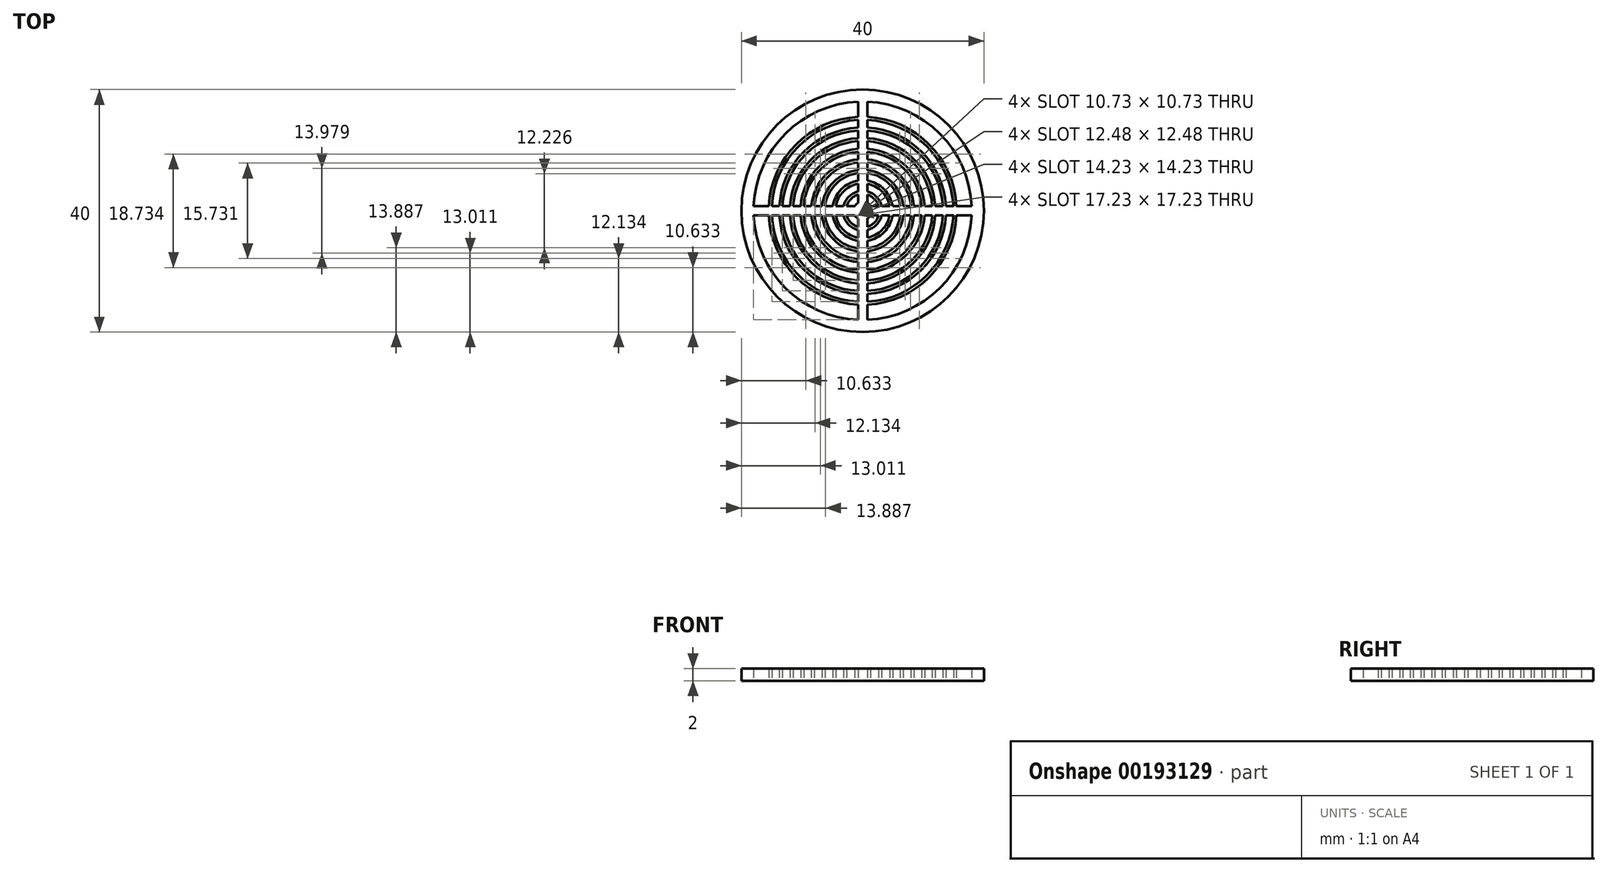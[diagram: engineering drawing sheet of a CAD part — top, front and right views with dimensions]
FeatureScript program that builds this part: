
annotation { "Feature Type Name" : "Feature", "Feature Type Description" : "" }
export const myFeature = defineFeature(function(context is Context, id is Id, definition is map)
    precondition{}
    {
        {
            var Q0;
            Q0=qCreatedBy(makeId("Top.planeOp"),FACE);
            var sketch = newSketch(context, id + "F0", { "sketchPlane" : qUnion([Q0])});
            skArc(sketch, "E0", {"start": v(0.75, -4.94) * mm, "mid": v(3.54, -3.54) * mm, "end": v(4.94, -0.75) * mm});
            skArc(sketch, "E1", {"start": v(0.75, -6.2) * mm, "mid": v(4.42, -4.42) * mm, "end": v(6.2, -0.75) * mm});
            skArc(sketch, "E2", {"start": v(0.75, -4.44) * mm, "mid": v(3.18, -3.18) * mm, "end": v(4.44, -0.75) * mm});
            skArc(sketch, "E3", {"start": v(0.75, -3.16) * mm, "mid": v(2.3, -2.3) * mm, "end": v(3.16, -0.75) * mm});
            skArc(sketch, "E4", {"start": v(0.75, -2.65) * mm, "mid": v(1.94, -1.94) * mm, "end": v(2.65, -0.75) * mm});
            skArc(sketch, "E5", {"start": v(0.75, -1.3) * mm, "mid": v(1.06, -1.06) * mm, "end": v(1.3, -0.75) * mm});
            skArc(sketch, "E6", {"start": v(0.75, -6.7) * mm, "mid": v(4.77, -4.77) * mm, "end": v(6.7, -0.75) * mm});
            skCircle(sketch, "E7", {"center": v(0, 0) * mm, "radius": 20 * mm});
            skLineSegment(sketch, "E8", {"start": v(-0.75, -17.98) * mm, "end": v(-0.75, -15.48) * mm});
            skLineSegment(sketch, "E9", {"start": v(-17.98, 0.75) * mm, "end": v(-15.48, 0.75) * mm});
            skLineSegment(sketch, "E10", {"start": v(34, 0.75) * mm, "end": v(34, -0.75) * mm});
            skLineSegment(sketch, "E11", {"start": v(34, -0.75) * mm, "end": v(19.99, -0.75) * mm});
            skArc(sketch, "E12", {"start": v(0.75, -7.96) * mm, "mid": v(5.66, -5.66) * mm, "end": v(7.96, -0.75) * mm});
            skArc(sketch, "E13", {"start": v(0.75, -8.47) * mm, "mid": v(6.01, -6.01) * mm, "end": v(8.47, -0.75) * mm});
            skArc(sketch, "E14", {"start": v(0.75, -9.72) * mm, "mid": v(6.9, -6.9) * mm, "end": v(9.72, -0.75) * mm});
            skArc(sketch, "E15", {"start": v(0.75, -10.22) * mm, "mid": v(7.25, -7.25) * mm, "end": v(10.22, -0.75) * mm});
            skArc(sketch, "E16", {"start": v(0.75, -11.48) * mm, "mid": v(8.13, -8.13) * mm, "end": v(11.48, -0.75) * mm});
            skArc(sketch, "E17", {"start": v(0.75, -11.98) * mm, "mid": v(8.49, -8.49) * mm, "end": v(11.98, -0.75) * mm});
            skArc(sketch, "E18", {"start": v(0.75, -13.23) * mm, "mid": v(9.37, -9.37) * mm, "end": v(13.23, -0.75) * mm});
            skArc(sketch, "E19", {"start": v(0.75, -13.73) * mm, "mid": v(9.72, -9.72) * mm, "end": v(13.73, -0.75) * mm});
            skArc(sketch, "E20", {"start": v(0.75, -14.98) * mm, "mid": v(10.6, -10.6) * mm, "end": v(14.98, -0.75) * mm});
            skArc(sketch, "E21", {"start": v(0.75, -15.48) * mm, "mid": v(10.96, -10.96) * mm, "end": v(15.48, -0.75) * mm});
            skArc(sketch, "E22", {"start": v(0.75, -17.98) * mm, "mid": v(12.73, -12.73) * mm, "end": v(17.98, -0.75) * mm});
            skLineSegment(sketch, "E23.trimOffspring", {"start": v(-0.75, -14.98) * mm, "end": v(-0.75, -13.73) * mm});
            skLineSegment(sketch, "E24.trimOffspring", {"start": v(0.75, -15.48) * mm, "end": v(0.75, -17.98) * mm});
            skLineSegment(sketch, "E25.trimOffspring", {"start": v(0.75, -13.73) * mm, "end": v(0.75, -14.98) * mm});
            skLineSegment(sketch, "E26.trimOffspring", {"start": v(-0.75, -13.23) * mm, "end": v(-0.75, -11.98) * mm});
            skLineSegment(sketch, "E27.trimOffspring", {"start": v(-0.75, -11.48) * mm, "end": v(-0.75, -10.22) * mm});
            skLineSegment(sketch, "E28.trimOffspring", {"start": v(-0.75, -9.72) * mm, "end": v(-0.75, -8.47) * mm});
            skLineSegment(sketch, "E29.trimOffspring", {"start": v(-0.75, -7.96) * mm, "end": v(-0.75, -6.7) * mm});
            skLineSegment(sketch, "E30.trimOffspring", {"start": v(-0.75, -6.2) * mm, "end": v(-0.75, -4.94) * mm});
            skLineSegment(sketch, "E31.trimOffspring", {"start": v(0.75, -6.7) * mm, "end": v(0.75, -7.96) * mm});
            skLineSegment(sketch, "E32.trimOffspring", {"start": v(0.75, -8.47) * mm, "end": v(0.75, -9.72) * mm});
            skLineSegment(sketch, "E33.trimOffspring", {"start": v(0.75, -10.22) * mm, "end": v(0.75, -11.48) * mm});
            skLineSegment(sketch, "E34.trimOffspring", {"start": v(0.75, -11.98) * mm, "end": v(0.75, -13.23) * mm});
            skLineSegment(sketch, "E35.trimOffspring", {"start": v(-0.75, -4.44) * mm, "end": v(-0.75, -3.16) * mm});
            skLineSegment(sketch, "E36.trimOffspring", {"start": v(0.75, -4.94) * mm, "end": v(0.75, -6.2) * mm});
            skLineSegment(sketch, "E37.trimOffspring", {"start": v(0.75, -3.16) * mm, "end": v(0.75, -4.44) * mm});
            skLineSegment(sketch, "E38.trimOffspring", {"start": v(-0.75, -2.65) * mm, "end": v(-0.75, -1.3) * mm});
            skLineSegment(sketch, "E39.trimOffspring", {"start": v(-1.3, -0.75) * mm, "end": v(-2.65, -0.75) * mm});
            skLineSegment(sketch, "E40.trimOffspring", {"start": v(-0.75, 1.3) * mm, "end": v(-0.75, 2.65) * mm});
            skLineSegment(sketch, "E41.trimOffspring", {"start": v(1.3, 0.75) * mm, "end": v(2.65, 0.75) * mm});
            skLineSegment(sketch, "E42.trimOffspring", {"start": v(0.75, -1.3) * mm, "end": v(0.75, -2.65) * mm});
            skArc(sketch, "E43.trimOffspring", {"start": v(-0.75, 1.3) * mm, "mid": v(-1.06, 1.06) * mm, "end": v(-1.3, 0.75) * mm});
            skArc(sketch, "E44.trimOffspring", {"start": v(-1.3, -0.75) * mm, "mid": v(-1.06, -1.06) * mm, "end": v(-0.75, -1.3) * mm});
            skArc(sketch, "E45.trimOffspring", {"start": v(1.3, 0.75) * mm, "mid": v(1.06, 1.06) * mm, "end": v(0.75, 1.3) * mm});
            skArc(sketch, "E46.trimOffspring", {"start": v(-2.65, -0.75) * mm, "mid": v(-1.94, -1.94) * mm, "end": v(-0.75, -2.65) * mm});
            skArc(sketch, "E47.trimOffspring", {"start": v(-3.16, -0.75) * mm, "mid": v(-2.3, -2.3) * mm, "end": v(-0.75, -3.16) * mm});
            skLineSegment(sketch, "E48.trimOffspring", {"start": v(-3.16, -0.75) * mm, "end": v(-4.44, -0.75) * mm});
            skLineSegment(sketch, "E49.trimOffspring", {"start": v(-2.65, 0.75) * mm, "end": v(-1.3, 0.75) * mm});
            skLineSegment(sketch, "E50.trimOffspring", {"start": v(-4.94, -0.75) * mm, "end": v(-6.2, -0.75) * mm});
            skLineSegment(sketch, "E51.trimOffspring", {"start": v(-4.44, 0.75) * mm, "end": v(-3.16, 0.75) * mm});
            skArc(sketch, "E52.trimOffspring", {"start": v(-4.44, -0.75) * mm, "mid": v(-3.18, -3.18) * mm, "end": v(-0.75, -4.44) * mm});
            skArc(sketch, "E53.trimOffspring", {"start": v(-4.94, -0.75) * mm, "mid": v(-3.54, -3.54) * mm, "end": v(-0.75, -4.94) * mm});
            skArc(sketch, "E54.trimOffspring", {"start": v(-6.2, -0.75) * mm, "mid": v(-4.42, -4.42) * mm, "end": v(-0.75, -6.2) * mm});
            skArc(sketch, "E55.trimOffspring", {"start": v(-6.7, -0.75) * mm, "mid": v(-4.77, -4.77) * mm, "end": v(-0.75, -6.7) * mm});
            skLineSegment(sketch, "E56.trimOffspring", {"start": v(-6.2, 0.75) * mm, "end": v(-4.94, 0.75) * mm});
            skLineSegment(sketch, "E57.trimOffspring", {"start": v(-6.7, -0.75) * mm, "end": v(-7.96, -0.75) * mm});
            skArc(sketch, "E58.trimOffspring", {"start": v(-7.96, -0.75) * mm, "mid": v(-5.66, -5.66) * mm, "end": v(-0.75, -7.96) * mm});
            skLineSegment(sketch, "E59.trimOffspring", {"start": v(-7.96, 0.75) * mm, "end": v(-6.7, 0.75) * mm});
            skArc(sketch, "E60.trimOffspring", {"start": v(-8.47, -0.75) * mm, "mid": v(-6.01, -6.01) * mm, "end": v(-0.75, -8.47) * mm});
            skLineSegment(sketch, "E61.trimOffspring", {"start": v(-8.47, -0.75) * mm, "end": v(-9.72, -0.75) * mm});
            skArc(sketch, "E62.trimOffspring", {"start": v(-9.72, -0.75) * mm, "mid": v(-6.9, -6.9) * mm, "end": v(-0.75, -9.72) * mm});
            skArc(sketch, "E63.trimOffspring", {"start": v(-10.22, -0.75) * mm, "mid": v(-7.25, -7.25) * mm, "end": v(-0.75, -10.22) * mm});
            skLineSegment(sketch, "E64.trimOffspring", {"start": v(-9.72, 0.75) * mm, "end": v(-8.47, 0.75) * mm});
            skLineSegment(sketch, "E65.trimOffspring", {"start": v(-10.22, -0.75) * mm, "end": v(-11.48, -0.75) * mm});
            skArc(sketch, "E66.trimOffspring", {"start": v(-11.48, -0.75) * mm, "mid": v(-8.13, -8.13) * mm, "end": v(-0.75, -11.48) * mm});
            skArc(sketch, "E67.trimOffspring", {"start": v(-11.98, -0.75) * mm, "mid": v(-8.49, -8.49) * mm, "end": v(-0.75, -11.98) * mm});
            skLineSegment(sketch, "E68.trimOffspring", {"start": v(-11.48, 0.75) * mm, "end": v(-10.22, 0.75) * mm});
            skLineSegment(sketch, "E69.trimOffspring", {"start": v(-11.98, -0.75) * mm, "end": v(-13.23, -0.75) * mm});
            skArc(sketch, "E70.trimOffspring", {"start": v(-13.23, -0.75) * mm, "mid": v(-9.37, -9.37) * mm, "end": v(-0.75, -13.23) * mm});
            skArc(sketch, "E71.trimOffspring", {"start": v(-13.73, -0.75) * mm, "mid": v(-9.72, -9.72) * mm, "end": v(-0.75, -13.73) * mm});
            skLineSegment(sketch, "E72.trimOffspring", {"start": v(-13.73, -0.75) * mm, "end": v(-14.98, -0.75) * mm});
            skLineSegment(sketch, "E73.trimOffspring", {"start": v(-13.23, 0.75) * mm, "end": v(-11.98, 0.75) * mm});
            skArc(sketch, "E74.trimOffspring", {"start": v(-17.98, -0.75) * mm, "mid": v(-12.73, -12.73) * mm, "end": v(-0.75, -17.98) * mm});
            skArc(sketch, "E75.trimOffspring", {"start": v(-14.98, -0.75) * mm, "mid": v(-10.6, -10.6) * mm, "end": v(-0.75, -14.98) * mm});
            skArc(sketch, "E76.trimOffspring", {"start": v(-15.48, -0.75) * mm, "mid": v(-10.96, -10.96) * mm, "end": v(-0.75, -15.48) * mm});
            skLineSegment(sketch, "E77.trimOffspring", {"start": v(-15.48, -0.75) * mm, "end": v(-17.98, -0.75) * mm});
            skLineSegment(sketch, "E78.trimOffspring", {"start": v(-14.98, 0.75) * mm, "end": v(-13.73, 0.75) * mm});
            skLineSegment(sketch, "E79.trimOffspring", {"start": v(3.16, 0.75) * mm, "end": v(4.44, 0.75) * mm});
            skLineSegment(sketch, "E80.trimOffspring", {"start": v(2.65, -0.75) * mm, "end": v(1.3, -0.75) * mm});
            skArc(sketch, "E81.trimOffspring", {"start": v(2.65, 0.75) * mm, "mid": v(1.94, 1.94) * mm, "end": v(0.75, 2.65) * mm});
            skArc(sketch, "E82.trimOffspring", {"start": v(3.16, 0.75) * mm, "mid": v(2.3, 2.3) * mm, "end": v(0.75, 3.16) * mm});
            skArc(sketch, "E83.trimOffspring", {"start": v(4.44, 0.75) * mm, "mid": v(3.18, 3.18) * mm, "end": v(0.75, 4.44) * mm});
            skArc(sketch, "E84.trimOffspring", {"start": v(4.94, 0.75) * mm, "mid": v(3.54, 3.54) * mm, "end": v(0.75, 4.94) * mm});
            skLineSegment(sketch, "E85.trimOffspring", {"start": v(4.94, 0.75) * mm, "end": v(6.2, 0.75) * mm});
            skLineSegment(sketch, "E86.trimOffspring", {"start": v(4.44, -0.75) * mm, "end": v(3.16, -0.75) * mm});
            skArc(sketch, "E87.trimOffspring", {"start": v(6.2, 0.75) * mm, "mid": v(4.42, 4.42) * mm, "end": v(0.75, 6.2) * mm});
            skArc(sketch, "E88.trimOffspring", {"start": v(6.7, 0.75) * mm, "mid": v(4.77, 4.77) * mm, "end": v(0.75, 6.7) * mm});
            skArc(sketch, "E89.trimOffspring", {"start": v(7.96, 0.75) * mm, "mid": v(5.66, 5.66) * mm, "end": v(0.75, 7.96) * mm});
            skArc(sketch, "E90.trimOffspring", {"start": v(8.47, 0.75) * mm, "mid": v(6.01, 6.01) * mm, "end": v(0.75, 8.47) * mm});
            skArc(sketch, "E91.trimOffspring", {"start": v(9.72, 0.75) * mm, "mid": v(6.9, 6.9) * mm, "end": v(0.75, 9.72) * mm});
            skArc(sketch, "E92.trimOffspring", {"start": v(10.22, 0.75) * mm, "mid": v(7.25, 7.25) * mm, "end": v(0.75, 10.22) * mm});
            skArc(sketch, "E93.trimOffspring", {"start": v(11.48, 0.75) * mm, "mid": v(8.13, 8.13) * mm, "end": v(0.75, 11.48) * mm});
            skArc(sketch, "E94.trimOffspring", {"start": v(11.98, 0.75) * mm, "mid": v(8.49, 8.49) * mm, "end": v(0.75, 11.98) * mm});
            skArc(sketch, "E95.trimOffspring", {"start": v(13.23, 0.75) * mm, "mid": v(9.37, 9.37) * mm, "end": v(0.75, 13.23) * mm});
            skArc(sketch, "E96.trimOffspring", {"start": v(13.73, 0.75) * mm, "mid": v(9.72, 9.72) * mm, "end": v(0.75, 13.73) * mm});
            skArc(sketch, "E97.trimOffspring", {"start": v(14.98, 0.75) * mm, "mid": v(10.6, 10.6) * mm, "end": v(0.75, 14.98) * mm});
            skArc(sketch, "E98.trimOffspring", {"start": v(15.48, 0.75) * mm, "mid": v(10.96, 10.96) * mm, "end": v(0.75, 15.48) * mm});
            skArc(sketch, "E99.trimOffspring", {"start": v(17.98, 0.75) * mm, "mid": v(12.73, 12.73) * mm, "end": v(0.75, 17.98) * mm});
            skLineSegment(sketch, "E100.trimOffspring", {"start": v(19.99, 0.75) * mm, "end": v(34, 0.75) * mm});
            skLineSegment(sketch, "E101.trimOffspring", {"start": v(17.98, -0.75) * mm, "end": v(15.48, -0.75) * mm});
            skLineSegment(sketch, "E102.trimOffspring", {"start": v(14.98, -0.75) * mm, "end": v(13.73, -0.75) * mm});
            skLineSegment(sketch, "E103.trimOffspring", {"start": v(15.48, 0.75) * mm, "end": v(17.98, 0.75) * mm});
            skLineSegment(sketch, "E104.trimOffspring", {"start": v(13.73, 0.75) * mm, "end": v(14.98, 0.75) * mm});
            skLineSegment(sketch, "E105.trimOffspring", {"start": v(13.23, -0.75) * mm, "end": v(11.98, -0.75) * mm});
            skLineSegment(sketch, "E106.trimOffspring", {"start": v(11.98, 0.75) * mm, "end": v(13.23, 0.75) * mm});
            skLineSegment(sketch, "E107.trimOffspring", {"start": v(11.48, -0.75) * mm, "end": v(10.22, -0.75) * mm});
            skLineSegment(sketch, "E108.trimOffspring", {"start": v(9.72, -0.75) * mm, "end": v(8.47, -0.75) * mm});
            skLineSegment(sketch, "E109.trimOffspring", {"start": v(10.22, 0.75) * mm, "end": v(11.48, 0.75) * mm});
            skLineSegment(sketch, "E110.trimOffspring", {"start": v(8.47, 0.75) * mm, "end": v(9.72, 0.75) * mm});
            skLineSegment(sketch, "E111.trimOffspring", {"start": v(7.96, -0.75) * mm, "end": v(6.7, -0.75) * mm});
            skLineSegment(sketch, "E112.trimOffspring", {"start": v(6.2, -0.75) * mm, "end": v(4.94, -0.75) * mm});
            skLineSegment(sketch, "E113.trimOffspring", {"start": v(6.7, 0.75) * mm, "end": v(7.96, 0.75) * mm});
            skArc(sketch, "E114.trimOffspring", {"start": v(-0.75, 2.65) * mm, "mid": v(-1.94, 1.94) * mm, "end": v(-2.65, 0.75) * mm});
            skArc(sketch, "E115.trimOffspring", {"start": v(-0.75, 3.16) * mm, "mid": v(-2.3, 2.3) * mm, "end": v(-3.16, 0.75) * mm});
            skArc(sketch, "E116.trimOffspring", {"start": v(-0.75, 4.44) * mm, "mid": v(-3.18, 3.18) * mm, "end": v(-4.44, 0.75) * mm});
            skArc(sketch, "E117.trimOffspring", {"start": v(-0.75, 4.94) * mm, "mid": v(-3.54, 3.54) * mm, "end": v(-4.94, 0.75) * mm});
            skArc(sketch, "E118.trimOffspring", {"start": v(-0.75, 6.2) * mm, "mid": v(-4.42, 4.42) * mm, "end": v(-6.2, 0.75) * mm});
            skArc(sketch, "E119.trimOffspring", {"start": v(-0.75, 6.7) * mm, "mid": v(-4.77, 4.77) * mm, "end": v(-6.7, 0.75) * mm});
            skArc(sketch, "E120.trimOffspring", {"start": v(-0.75, 7.96) * mm, "mid": v(-5.66, 5.66) * mm, "end": v(-7.96, 0.75) * mm});
            skArc(sketch, "E121.trimOffspring", {"start": v(-0.75, 8.47) * mm, "mid": v(-6.01, 6.01) * mm, "end": v(-8.47, 0.75) * mm});
            skArc(sketch, "E122.trimOffspring", {"start": v(-0.75, 9.72) * mm, "mid": v(-6.9, 6.9) * mm, "end": v(-9.72, 0.75) * mm});
            skArc(sketch, "E123.trimOffspring", {"start": v(-0.75, 10.22) * mm, "mid": v(-7.25, 7.25) * mm, "end": v(-10.22, 0.75) * mm});
            skArc(sketch, "E124.trimOffspring", {"start": v(-0.75, 11.48) * mm, "mid": v(-8.13, 8.13) * mm, "end": v(-11.48, 0.75) * mm});
            skArc(sketch, "E125.trimOffspring", {"start": v(-0.75, 11.98) * mm, "mid": v(-8.49, 8.49) * mm, "end": v(-11.98, 0.75) * mm});
            skArc(sketch, "E126.trimOffspring", {"start": v(-0.75, 13.23) * mm, "mid": v(-9.37, 9.37) * mm, "end": v(-13.23, 0.75) * mm});
            skArc(sketch, "E127.trimOffspring", {"start": v(-0.75, 13.73) * mm, "mid": v(-9.72, 9.72) * mm, "end": v(-13.73, 0.75) * mm});
            skArc(sketch, "E128.trimOffspring", {"start": v(-0.75, 14.98) * mm, "mid": v(-10.6, 10.6) * mm, "end": v(-14.98, 0.75) * mm});
            skArc(sketch, "E129.trimOffspring", {"start": v(-0.75, 15.48) * mm, "mid": v(-10.96, 10.96) * mm, "end": v(-15.48, 0.75) * mm});
            skArc(sketch, "E130.trimOffspring", {"start": v(-0.75, 17.98) * mm, "mid": v(-12.73, 12.73) * mm, "end": v(-17.98, 0.75) * mm});
            skLineSegment(sketch, "E131.trimOffspring", {"start": v(0.75, 17.98) * mm, "end": v(0.75, 15.48) * mm});
            skPoint(sketch, "E132.start.orphan", {"position": v(-0.75, 25.89) * mm});
            skPoint(sketch, "E133.start.orphan", {"position": v(0.75, 25.89) * mm});
            skLineSegment(sketch, "E134.trimOffspring", {"start": v(-0.75, 15.48) * mm, "end": v(-0.75, 17.98) * mm});
            skLineSegment(sketch, "E135.trimOffspring", {"start": v(0.75, 14.98) * mm, "end": v(0.75, 13.73) * mm});
            skLineSegment(sketch, "E136.trimOffspring", {"start": v(-0.75, 13.73) * mm, "end": v(-0.75, 14.98) * mm});
            skLineSegment(sketch, "E137.trimOffspring", {"start": v(0.75, 13.23) * mm, "end": v(0.75, 11.98) * mm});
            skLineSegment(sketch, "E138.trimOffspring", {"start": v(-0.75, 11.98) * mm, "end": v(-0.75, 13.23) * mm});
            skLineSegment(sketch, "E139.trimOffspring", {"start": v(0.75, 11.48) * mm, "end": v(0.75, 10.22) * mm});
            skLineSegment(sketch, "E140.trimOffspring", {"start": v(-0.75, 10.22) * mm, "end": v(-0.75, 11.48) * mm});
            skLineSegment(sketch, "E141.trimOffspring", {"start": v(0.75, 9.72) * mm, "end": v(0.75, 8.47) * mm});
            skLineSegment(sketch, "E142.trimOffspring", {"start": v(0.75, 7.96) * mm, "end": v(0.75, 6.7) * mm});
            skLineSegment(sketch, "E143.trimOffspring", {"start": v(-0.75, 8.47) * mm, "end": v(-0.75, 9.72) * mm});
            skLineSegment(sketch, "E144.trimOffspring", {"start": v(-0.75, 6.7) * mm, "end": v(-0.75, 7.96) * mm});
            skLineSegment(sketch, "E145.trimOffspring", {"start": v(0.75, 6.2) * mm, "end": v(0.75, 4.94) * mm});
            skLineSegment(sketch, "E146.trimOffspring", {"start": v(0.75, 4.44) * mm, "end": v(0.75, 3.16) * mm});
            skLineSegment(sketch, "E147.trimOffspring", {"start": v(-0.75, 4.94) * mm, "end": v(-0.75, 6.2) * mm});
            skLineSegment(sketch, "E148.trimOffspring", {"start": v(-0.75, 3.16) * mm, "end": v(-0.75, 4.44) * mm});
            skLineSegment(sketch, "E149.trimOffspring", {"start": v(0.75, 2.65) * mm, "end": v(0.75, 1.3) * mm});
            skSolve(sketch);
        }
        {
            var Q0;
            Q0=makeQuery(id+"F0.imprint","IMPRINT",FACE,{"disambiguationData":[TD([[makeQuery(id+"F0.imprint","IMPRINT",EDGE,{"derivedFrom":sQuery(id+"F0.wireOp",EDGE,"E0")}),1.0]])]});
            extrude(context, id + "F1", {"entities" : qUnion([Q0]), "depth" : 2 * mm});
        }
    });
